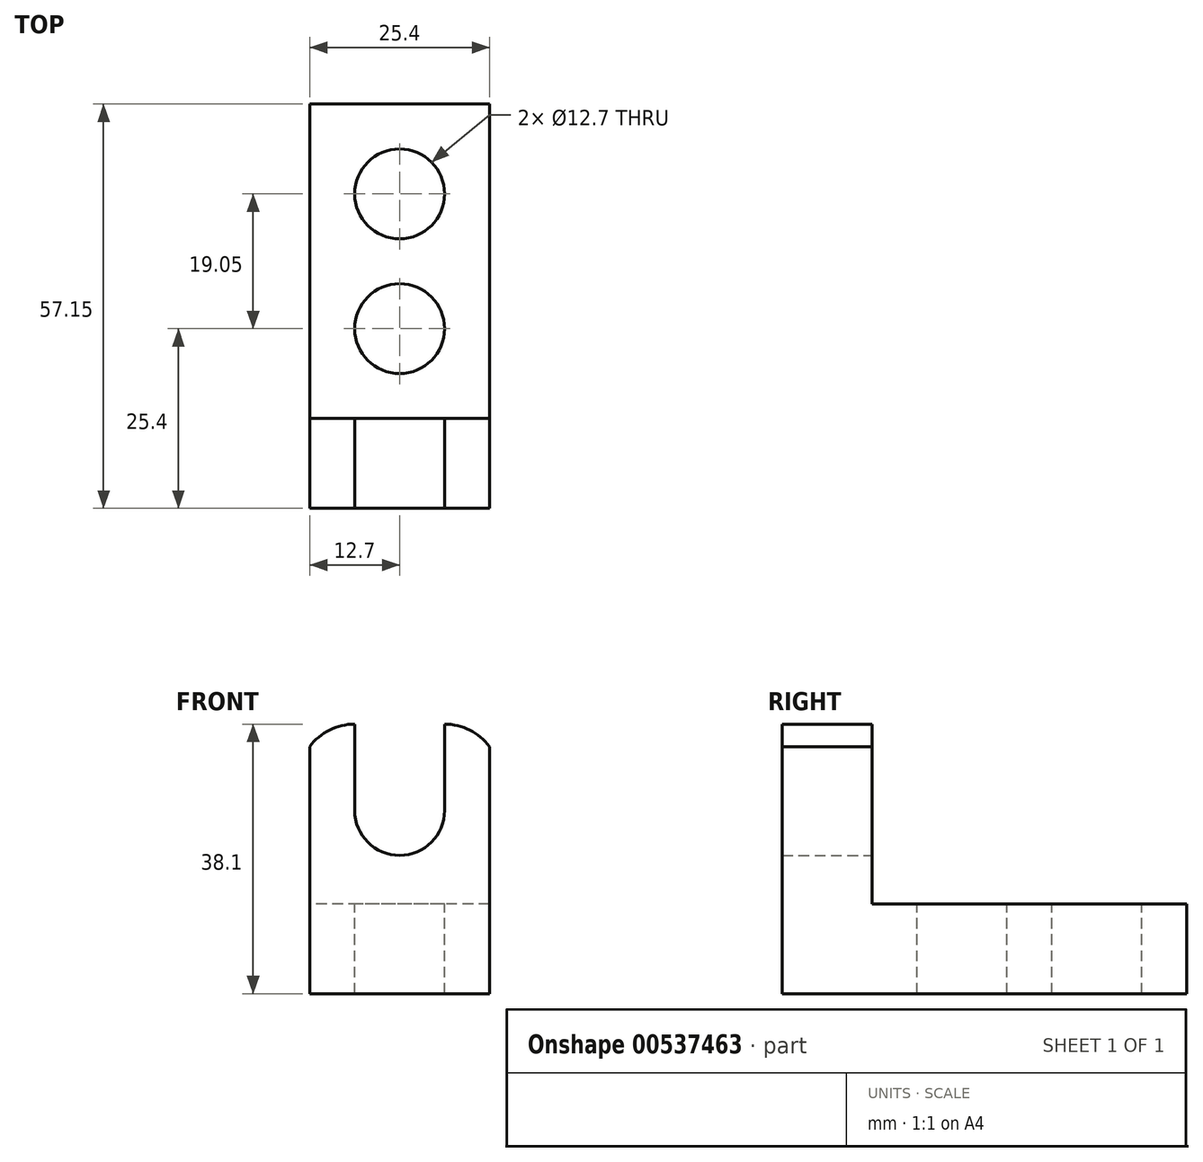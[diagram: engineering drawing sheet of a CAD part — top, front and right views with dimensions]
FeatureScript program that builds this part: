
annotation { "Feature Type Name" : "Feature", "Feature Type Description" : "" }
export const myFeature = defineFeature(function(context is Context, id is Id, definition is map)
    precondition{}
    {
        {
            var Q0;
            Q0=qCreatedBy(makeId("Right.planeOp"),FACE);
            var sketch = newSketch(context, id + "F0", { "sketchPlane" : qUnion([Q0])});
            skLineSegment(sketch, "E0", {"start": v(0, 0) * mm, "end": v(0, 38.1) * mm});
            skLineSegment(sketch, "E1", {"start": v(0, 38.1) * mm, "end": v(12.7, 38.1) * mm});
            skLineSegment(sketch, "E2", {"start": v(12.7, 38.1) * mm, "end": v(12.7, 12.7) * mm});
            skLineSegment(sketch, "E3", {"start": v(12.7, 12.7) * mm, "end": v(57.15, 12.7) * mm});
            skLineSegment(sketch, "E4", {"start": v(57.15, 12.7) * mm, "end": v(57.15, 0) * mm});
            skLineSegment(sketch, "E5", {"start": v(57.15, 0) * mm, "end": v(0, 0) * mm});
            skSolve(sketch);
        }
        {
            var Q0;
            Q0 = qSketchRegion(id + "F0", true);
            extrude(context, id + "F1", {"entities" : qUnion([Q0]), "depth" : 25.4 * mm, "offsetDistance" : 25.4 * mm});
        }
        {
            var Q0;
            Q0=makeQuery(id+"F1.opExtrude","SWEPT_FACE",FACE,{"disambiguationData":[OSD([sQuery(id+"F0.wireOp",EDGE,"E2")])]});
            var sketch = newSketch(context, id + "F2", { "sketchPlane" : qUnion([Q0])});
            skCircle(sketch, "E6", {"center": v(-12.7, 25.9) * mm, "radius": 6.35 * mm});
            skPoint(sketch, "E6.centerSnap0", {"position": v(-12.7, 38.1) * mm});
            skLineSegment(sketch, "E7", {"start": v(-6.35, 25.9) * mm, "end": v(-6.35, 38.1) * mm});
            skLineSegment(sketch, "E8", {"start": v(-19.05, 25.9) * mm, "end": v(-19.05, 38.1) * mm});
            skSolve(sketch);
        }
        {
            var Q0;
            Q0 = qSketchRegion(id + "F2", true);
            var Q1;
            {var subQ0=sQuery(id+"F2.wireOp",EDGE,"E7");Q1=makeQuery(id+"F2.imprint","IMPRINT",FACE,{"disambiguationData":[TD([[makeQuery(id+"F2.imprint","IMPRINT",EDGE,{"derivedFrom":subQ0}),1.0]])]});}
            extrude(context, id + "F3", {"entities" : qUnion([Q0, Q1]), "operationType" : NewBodyOperationType.REMOVE, "oppositeDirection" : true, "depth" : 25.4 * mm, "offsetDistance" : 25.4 * mm});
        }
        {
            var Q0;
            Q0=makeQuery(id+"F1.opExtrude","SWEPT_FACE",FACE,{"disambiguationData":[OSD([sQuery(id+"F0.wireOp",EDGE,"E2")])]});
            var sketch = newSketch(context, id + "F4", { "sketchPlane" : qUnion([Q0])});
            skArc(sketch, "E9", {"start": v(-19.05, 38.1) * mm, "mid": v(-26.15, 33.71) * mm, "end": v(-25.4, 25.4) * mm});
            skSolve(sketch);
        }
        {
            var Q0;
            Q0 = qSketchRegion(id + "F4", true);
            var Q1;
            {var subQ1=sQuery(id+"F0.wireOp",EDGE,"E2");var subQ2=sQuery(id+"F0.wireOp",EDGE,"E1");var subQ3=sQuery(id+"F2.wireOp",EDGE,"E8");var subQ4=makeQuery(id+"F3.boolean.opBoolean","SPLIT",EDGE,{"disambiguationData":[TD([makeQuery(id+"F3.opExtrude","SWEPT_FACE",FACE,{"disambiguationData":[OSD([subQ3])]})])],"derivedFrom":makeQuery(id+"F1.opExtrude","SWEPT_EDGE",EDGE,{"disambiguationData":[OSD([subQ2,subQ1])]})});Q1=makeQuery(id+"F4.imprint","IMPRINT",FACE,{"disambiguationData":[TD([[makeQuery(id+"F4.imprint","IMPRINT",EDGE,{"derivedFrom":subQ4}),-1.0]])]});}
            extrude(context, id + "F5", {"entities" : qUnion([Q0, Q1]), "operationType" : NewBodyOperationType.REMOVE, "oppositeDirection" : true, "depth" : 25.4 * mm, "offsetDistance" : 25.4 * mm});
        }
        {
            var Q0;
            Q0=makeQuery(id+"F1.opExtrude","SWEPT_FACE",FACE,{"disambiguationData":[OSD([sQuery(id+"F0.wireOp",EDGE,"E2")])]});
            var sketch = newSketch(context, id + "F6", { "sketchPlane" : qUnion([Q0])});
            skArc(sketch, "E10", {"start": v(0, 25.4) * mm, "mid": v(0.75, 33.71) * mm, "end": v(-6.35, 38.1) * mm});
            skSolve(sketch);
        }
        {
            var Q0;
            Q0 = qSketchRegion(id + "F6", true);
            var Q1;
            {var subQ1=sQuery(id+"F0.wireOp",EDGE,"E2");var subQ2=sQuery(id+"F0.wireOp",EDGE,"E1");var subQ3=sQuery(id+"F2.wireOp",EDGE,"E7");var subQ4=makeQuery(id+"F3.boolean.opBoolean","SPLIT",EDGE,{"disambiguationData":[TD([makeQuery(id+"F3.opExtrude","SWEPT_FACE",FACE,{"disambiguationData":[OSD([subQ3])]})])],"derivedFrom":makeQuery(id+"F1.opExtrude","SWEPT_EDGE",EDGE,{"disambiguationData":[OSD([subQ2,subQ1])]})});Q1=makeQuery(id+"F6.imprint","IMPRINT",FACE,{"disambiguationData":[TD([[makeQuery(id+"F6.imprint","IMPRINT",EDGE,{"derivedFrom":subQ4}),-1.0]])]});}
            extrude(context, id + "F7", {"entities" : qUnion([Q0, Q1]), "operationType" : NewBodyOperationType.REMOVE, "oppositeDirection" : true, "depth" : 25.4 * mm, "offsetDistance" : 25.4 * mm});
        }
        {
            var Q0;
            Q0=makeQuery(id+"F1.opExtrude","SWEPT_FACE",FACE,{"disambiguationData":[OSD([sQuery(id+"F0.wireOp",EDGE,"E3")])]});
            var sketch = newSketch(context, id + "F8", { "sketchPlane" : qUnion([Q0])});
            skCircle(sketch, "E11", {"center": v(12.7, 25.4) * mm, "radius": 6.35 * mm});
            skCircle(sketch, "E12", {"center": v(12.7, 44.45) * mm, "radius": 6.35 * mm});
            skLineSegment(sketch, "E13.0.0", {"start": v(0, 57.15) * mm, "end": v(0, 12.7) * mm});
            skLineSegment(sketch, "E13.0.1", {"start": v(0, 12.7) * mm, "end": v(25.4, 12.7) * mm});
            skLineSegment(sketch, "E13.0.2", {"start": v(25.4, 12.7) * mm, "end": v(25.4, 57.15) * mm});
            skLineSegment(sketch, "E13.0.3", {"start": v(25.4, 57.15) * mm, "end": v(0, 57.15) * mm});
            skSolve(sketch);
        }
        {
            var Q0;
            Q0=makeQuery(id+"F8.imprint","IMPRINT",FACE,{"disambiguationData":[TD([[makeQuery(id+"F8.imprint","IMPRINT",EDGE,{"derivedFrom":sQuery(id+"F8.wireOp",EDGE,"E12")}),1.0]])]});
            var Q1;
            Q1=makeQuery(id+"F8.imprint","IMPRINT",FACE,{"disambiguationData":[TD([[makeQuery(id+"F8.imprint","IMPRINT",EDGE,{"derivedFrom":sQuery(id+"F8.wireOp",EDGE,"E11")}),1.0]])]});
            extrude(context, id + "F9", {"entities" : qUnion([Q0, Q1]), "operationType" : NewBodyOperationType.REMOVE, "oppositeDirection" : true, "depth" : 25.4 * mm, "offsetDistance" : 25.4 * mm});
        }
    });
